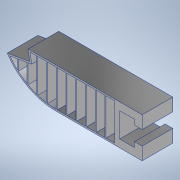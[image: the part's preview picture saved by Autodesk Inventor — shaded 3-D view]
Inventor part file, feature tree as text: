
AUTODESK INVENTOR PART (.ipt)
format: ipt  version: 2022 (Build 260153000, 153)  size: 275,968 bytes
history: native  units: mm
features: extrude x5, sketch x4, fillet x1, shell x1, projected_geometry x1
ambient origin geometry x8: Origin, YZ Plane, XZ Plane, XY Plane, X Axis, Y Axis, Z Axis, Center Point
bodies: Body1 (feature_tree)
feature tree (12):
  extrude  "Extrusion2"  Depth=5.8mm
  extrude  "Extrusion5"  Depth=12.0mm TaperAngle=0.0deg
  fillet  "Fillet2"  Radius=45.0mm
  shell  "Shell1"  Thickness=15.6mm
  extrude  "Extrusion7"  TaperAngle=0.0deg  [1 undecoded]
  extrude  "Extrusion8"  Depth=9.6mm
  extrude  "Extrusion9"  Depth=12.0mm
  sketch  "Sketch8"  dims[d41=5.8mm d48=44.0mm]
  sketch  "Sketch13"  dims[d50=3.0mm d56=12.0mm d57=0.0mm d63=45.0mm d67=15.6mm d71=0.0mm]
  sketch  "Sketch14"  dims[d80=17.453293mm d82=0.0mm d83=0.0mm]
  projected_geometry  "Projected Loop1"
  sketch  "Sketch15"  dims[d87=5.6mm d88=9.6mm d95=4.0mm d96=9.0mm d97=15.6mm d98=23.0mm d99=0.62mm d100=12.0mm d101=0.0mm d102=10.747401mm d103=12.0mm d104=0.0mm d105=0.38mm d106=3.81mm d107=0.38mm d1=0.38mm d108=0.38mm d109=0.38mm d110=0.38mm d111=0.38mm d112=0.38mm d113=0.38mm d116=3.81mm d117=3.81mm d118=0.38mm d119=0.38mm d120=3.81mm d121=3.81mm d122=3.81mm d123=3.81mm d124=3.81mm d125=3.81mm d126=3.81mm d127=12.0mm d128=0.0mm]
note: 1 required parameter value undecoded (feature->parameter linkage not recoverable at this tier; creation-order binding heuristic only, values carry confidence <= 0.55)
